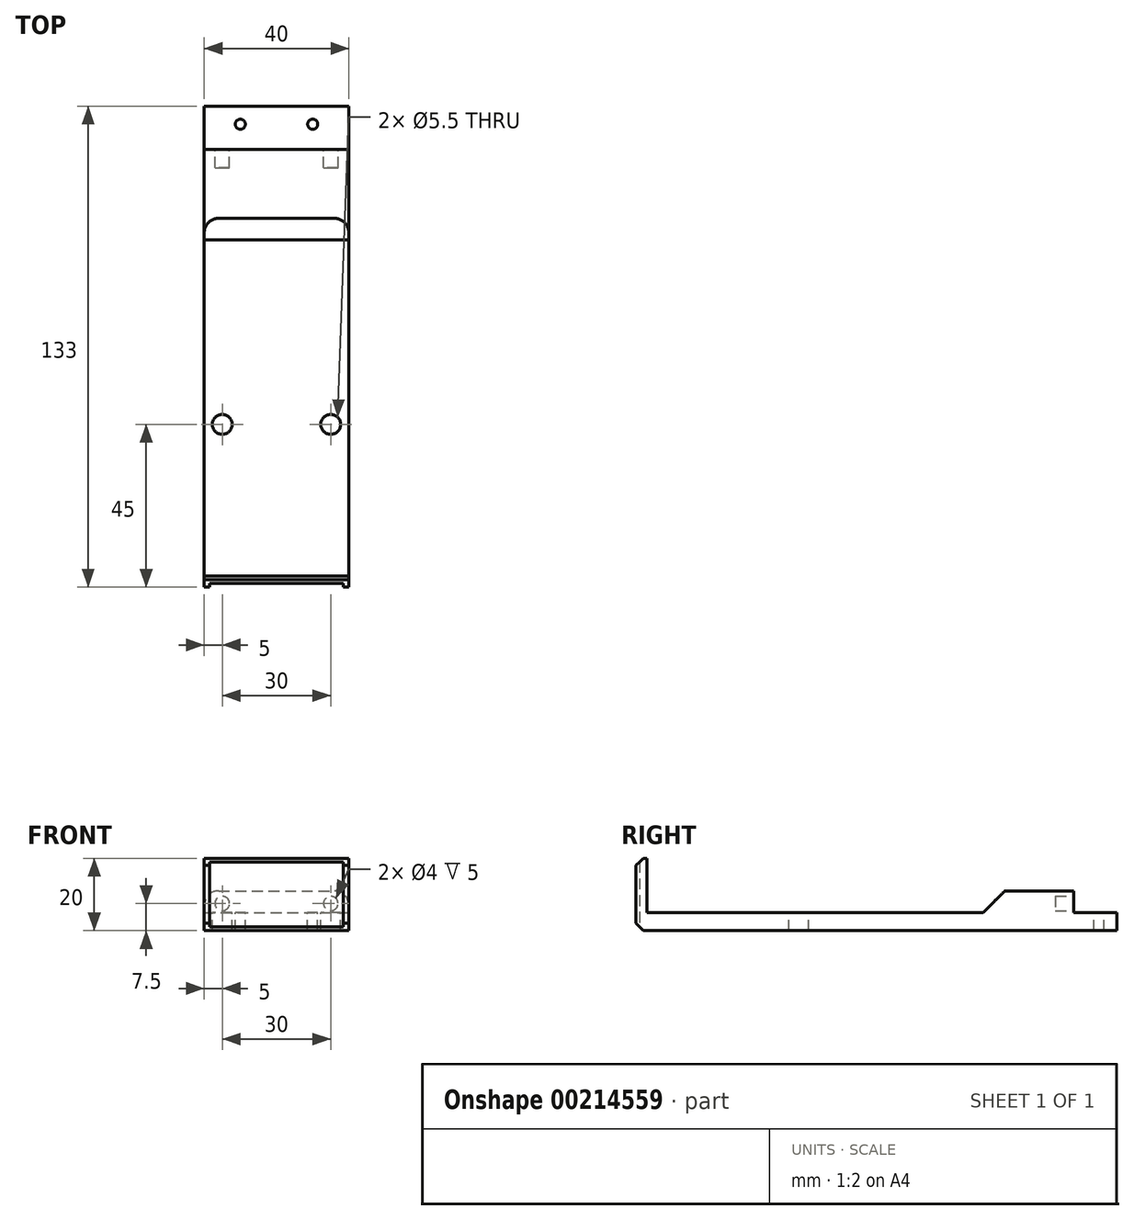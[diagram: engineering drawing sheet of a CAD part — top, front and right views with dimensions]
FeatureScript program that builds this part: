
annotation { "Feature Type Name" : "Feature", "Feature Type Description" : "" }
export const myFeature = defineFeature(function(context is Context, id is Id, definition is map)
    precondition{}
    {
        {
            var Q0;
            Q0=qCreatedBy(makeId("Top.planeOp"),FACE);
            var sketch = newSketch(context, id + "F0", { "sketchPlane" : qUnion([Q0])});
            skLineSegment(sketch, "E0.bottom", {"start": v(-20, 66) * mm, "end": v(20, 66) * mm});
            skLineSegment(sketch, "E0.top", {"start": v(-20, -66) * mm, "end": v(20, -66) * mm});
            skLineSegment(sketch, "E0.left", {"start": v(-20, 66) * mm, "end": v(-20, -66) * mm});
            skLineSegment(sketch, "E0.right", {"start": v(20, 66) * mm, "end": v(20, -66) * mm});
            skSolve(sketch);
        }
        {
            var Q0;
            Q0=makeQuery(id+"F0.imprint","IMPRINT",FACE,{"disambiguationData":[TD([[makeQuery(id+"F0.imprint","IMPRINT",EDGE,{"derivedFrom":sQuery(id+"F0.wireOp",EDGE,"E0.bottom")}),-1.0]])]});
            extrude(context, id + "F1", {"entities" : qUnion([Q0]), "depth" : 5 * mm});
        }
        {
            var Q0;
            Q0=makeQuery(id+"F1.opExtrude","CAP_FACE",FACE,{"disambiguationData":[OSD([sQuery(id+"F0.wireOp",EDGE,"E0.bottom"),sQuery(id+"F0.wireOp",EDGE,"E0.top"),sQuery(id+"F0.wireOp",EDGE,"E0.left"),sQuery(id+"F0.wireOp",EDGE,"E0.right")])],"isStart":false});
            var sketch = newSketch(context, id + "F2", { "sketchPlane" : qUnion([Q0])});
            skLineSegment(sketch, "E1.bottom", {"start": v(-20, -66) * mm, "end": v(20, -66) * mm});
            skLineSegment(sketch, "E1.top", {"start": v(-20, -64) * mm, "end": v(20, -64) * mm});
            skLineSegment(sketch, "E1.left", {"start": v(-20, -66) * mm, "end": v(-20, -64) * mm});
            skLineSegment(sketch, "E1.right", {"start": v(20, -66) * mm, "end": v(20, -64) * mm});
            skPoint(sketch, "E2", {"position": v(-15, -22) * mm});
            skPoint(sketch, "E3", {"position": v(15, -22) * mm});
            skSolve(sketch);
        }
        {
            var Q0;
            Q0=makeQuery(id+"F2.imprint","IMPRINT",FACE,{"disambiguationData":[TD([[makeQuery(id+"F2.imprint","IMPRINT",EDGE,{"derivedFrom":sQuery(id+"F2.wireOp",EDGE,"E1.bottom")}),1.0]])]});
            extrude(context, id + "F3", {"entities" : qUnion([Q0]), "operationType" : NewBodyOperationType.ADD, "depth" : 15 * mm});
        }
        {
            var Q0;
            Q0=sQuery(id+"F2.wireOp",VERTEX,"E2");
            var Q1;
            Q1=sQuery(id+"F2.wireOp",VERTEX,"E3");
            var Q2;
            Q2=makeQuery(id+"F1.opExtrude","SWEPT_BODY",BODY,{"disambiguationData":[OSD([sQuery(id+"F0.wireOp",EDGE,"E0.bottom"),sQuery(id+"F0.wireOp",EDGE,"E0.top"),sQuery(id+"F0.wireOp",EDGE,"E0.left"),sQuery(id+"F0.wireOp",EDGE,"E0.right")])]});
            hole(context, id + "F4", {"style" : HoleStyle.SIMPLE, "endStyle" : HoleEndStyle.BLIND, "holeDiameter" : 5.5 * mm, "holeDepth" : 8 * mm, "locations" : qUnion([Q0, Q1]), "scope" : qUnion([Q2])});
        }
        {
            var Q0;
            Q0=makeQuery(id+"F3.opExtrude","CAP_EDGE",EDGE,{"disambiguationData":[OSD([sQuery(id+"F2.wireOp",EDGE,"E1.bottom")])],"isStart":false});
            var Q1;
            Q1=makeQuery(id+"F4.hole-1.boolean.opBoolean","INTERSECT",EDGE,{"derivedFrom":[makeQuery(id+"F1.opExtrude","CAP_FACE",FACE,{"disambiguationData":[OSD([sQuery(id+"F0.wireOp",EDGE,"E0.bottom"),sQuery(id+"F0.wireOp",EDGE,"E0.top"),sQuery(id+"F0.wireOp",EDGE,"E0.left"),sQuery(id+"F0.wireOp",EDGE,"E0.right")])],"isStart":true}),makeQuery(id+"F4.hole-1.opRevolve","SWEPT_FACE",FACE,{"disambiguationData":[OSD([sQuery(id+"F4.hole-1.sketch.wireOp",EDGE,"core_line_2")])]})]});
            var Q2;
            Q2=makeQuery(id+"F4.hole-0.boolean.opBoolean","INTERSECT",EDGE,{"derivedFrom":[makeQuery(id+"F1.opExtrude","CAP_FACE",FACE,{"disambiguationData":[OSD([sQuery(id+"F0.wireOp",EDGE,"E0.bottom"),sQuery(id+"F0.wireOp",EDGE,"E0.top"),sQuery(id+"F0.wireOp",EDGE,"E0.left"),sQuery(id+"F0.wireOp",EDGE,"E0.right")])],"isStart":true}),makeQuery(id+"F4.hole-0.opRevolve","SWEPT_FACE",FACE,{"disambiguationData":[OSD([sQuery(id+"F4.hole-0.sketch.wireOp",EDGE,"core_line_2")])]})]});
            var Q3;
            Q3=makeQuery(id+"F1.opExtrude","CAP_EDGE",EDGE,{"disambiguationData":[OSD([sQuery(id+"F0.wireOp",EDGE,"E0.top")])],"isStart":true});
            chamfer(context, id + "F5", {"entities" : qUnion([Q0, Q1, Q2, Q3]), "width" : 1 * mm, "tangentPropagation" : true});
        }
        {
            var Q0;
            {var subQ0=sQuery(id+"F2.wireOp",EDGE,"E1.top");Q0=makeQuery(id+"F2.imprint","IMPRINT",FACE,{"disambiguationData":[TD([[makeQuery(id+"F2.imprint","IMPRINT",EDGE,{"derivedFrom":subQ0}),1.0]])]});}
            var sketch = newSketch(context, id + "F6", { "sketchPlane" : qUnion([Q0])});
            skLineSegment(sketch, "E4.bottom", {"start": v(-20, 54) * mm, "end": v(20, 54) * mm});
            skLineSegment(sketch, "E4.top", {"start": v(-20, 29) * mm, "end": v(20, 29) * mm});
            skLineSegment(sketch, "E4.left", {"start": v(-20, 54) * mm, "end": v(-20, 29) * mm});
            skLineSegment(sketch, "E4.right", {"start": v(20, 54) * mm, "end": v(20, 29) * mm});
            skPoint(sketch, "E5", {"position": v(-10, 61) * mm});
            skPoint(sketch, "E6", {"position": v(10, 61) * mm});
            skSolve(sketch);
        }
        {
            var Q0;
            Q0=makeQuery(id+"F6.imprint","IMPRINT",FACE,{"disambiguationData":[TD([[makeQuery(id+"F6.imprint","IMPRINT",EDGE,{"derivedFrom":sQuery(id+"F6.wireOp",EDGE,"E4.bottom")}),-1.0]])]});
            extrude(context, id + "F7", {"entities" : qUnion([Q0]), "operationType" : NewBodyOperationType.ADD, "depth" : 6 * mm});
        }
        {
            var Q0;
            Q0=makeQuery(id+"F7.opExtrude","SWEPT_FACE",FACE,{"disambiguationData":[OSD([sQuery(id+"F6.wireOp",EDGE,"E4.bottom")])]});
            var sketch = newSketch(context, id + "F8", { "sketchPlane" : qUnion([Q0])});
            skCircle(sketch, "E7", {"center": v(-15, 7.5) * mm, "radius": 2 * mm});
            skCircle(sketch, "E8", {"center": v(15, 7.5) * mm, "radius": 2 * mm});
            skSolve(sketch);
        }
        {
            var Q0;
            Q0=makeQuery(id+"F8.imprint","IMPRINT",FACE,{"disambiguationData":[TD([[makeQuery(id+"F8.imprint","IMPRINT",EDGE,{"derivedFrom":sQuery(id+"F8.wireOp",EDGE,"E7")}),1.0]])]});
            var Q1;
            Q1=makeQuery(id+"F8.imprint","IMPRINT",FACE,{"disambiguationData":[TD([[makeQuery(id+"F8.imprint","IMPRINT",EDGE,{"derivedFrom":sQuery(id+"F8.wireOp",EDGE,"E8")}),1.0]])]});
            extrude(context, id + "F9", {"entities" : qUnion([Q0, Q1]), "operationType" : NewBodyOperationType.REMOVE, "oppositeDirection" : true, "depth" : 5 * mm});
        }
        {
            var Q0;
            Q0=makeQuery(id+"F7.opExtrude","CAP_EDGE",EDGE,{"disambiguationData":[OSD([sQuery(id+"F6.wireOp",EDGE,"E4.top")])],"isStart":false});
            chamfer(context, id + "F10", {"entities" : qUnion([Q0]), "width" : 6 * mm, "tangentPropagation" : true});
        }
        {
            var Q0;
            Q0=makeQuery(id+"F7.opExtrude","CAP_EDGE",EDGE,{"disambiguationData":[OSD([sQuery(id+"F6.wireOp",EDGE,"E4.left")])],"isStart":false});
            var Q1;
            Q1=makeQuery(id+"F7.opExtrude","CAP_EDGE",EDGE,{"disambiguationData":[OSD([sQuery(id+"F6.wireOp",EDGE,"E4.right")])],"isStart":false});
            fillet(context, id + "F11", {"entities" : qUnion([Q0, Q1]), "radius" : 4 * mm, "tangentPropagation" : true, "allowEdgeOverflow" : false});
        }
        {
            var Q0;
            Q0=sQuery(id+"F6.wireOp",VERTEX,"E6");
            var Q1;
            Q1=sQuery(id+"F6.wireOp",VERTEX,"E5");
            var Q2;
            Q2=makeQuery(id+"F1.opExtrude","SWEPT_BODY",BODY,{"disambiguationData":[OSD([sQuery(id+"F0.wireOp",EDGE,"E0.bottom"),sQuery(id+"F0.wireOp",EDGE,"E0.top"),sQuery(id+"F0.wireOp",EDGE,"E0.left"),sQuery(id+"F0.wireOp",EDGE,"E0.right")])]});
            hole(context, id + "F12", {"style" : HoleStyle.SIMPLE, "endStyle" : HoleEndStyle.BLIND, "holeDiameter" : 2.8 * mm, "holeDepth" : 8 * mm, "locations" : qUnion([Q0, Q1]), "scope" : qUnion([Q2])});
        }
        {
            var Q0;
            Q0=makeQuery(id+"F3.boolean.opBoolean","MERGE",FACE,{"derivedFrom":[makeQuery(id+"F1.opExtrude","SWEPT_FACE",FACE,{"disambiguationData":[OSD([sQuery(id+"F0.wireOp",EDGE,"E0.top")])]}),makeQuery(id+"F3.opExtrude","SWEPT_FACE",FACE,{"disambiguationData":[OSD([sQuery(id+"F2.wireOp",EDGE,"E1.bottom")])]})]});
            var sketch = newSketch(context, id + "F13", { "sketchPlane" : qUnion([Q0])});
            skLineSegment(sketch, "E9.bottom", {"start": v(-20, 19) * mm, "end": v(-18.5, 19) * mm});
            skLineSegment(sketch, "E9.top", {"start": v(-20, 1) * mm, "end": v(-18.5, 1) * mm});
            skLineSegment(sketch, "E9.left", {"start": v(-20, 19) * mm, "end": v(-20, 1) * mm});
            skLineSegment(sketch, "E9.right", {"start": v(-18.5, 19) * mm, "end": v(-18.5, 1) * mm});
            skLineSegment(sketch, "E10.bottom", {"start": v(20, 19) * mm, "end": v(18.5, 19) * mm});
            skLineSegment(sketch, "E10.top", {"start": v(20, 1) * mm, "end": v(18.5, 1) * mm});
            skLineSegment(sketch, "E10.left", {"start": v(20, 19) * mm, "end": v(20, 1) * mm});
            skLineSegment(sketch, "E10.right", {"start": v(18.5, 19) * mm, "end": v(18.5, 1) * mm});
            skSolve(sketch);
        }
        {
            var Q0;
            Q0=makeQuery(id+"F13.imprint","IMPRINT",FACE,{"disambiguationData":[TD([[makeQuery(id+"F13.imprint","IMPRINT",EDGE,{"derivedFrom":sQuery(id+"F13.wireOp",EDGE,"E9.bottom")}),1.0]])]});
            var Q1;
            Q1=makeQuery(id+"F13.imprint","IMPRINT",FACE,{"disambiguationData":[TD([[makeQuery(id+"F13.imprint","IMPRINT",EDGE,{"derivedFrom":sQuery(id+"F13.wireOp",EDGE,"E10.bottom")}),1.0]])]});
            extrude(context, id + "F14", {"entities" : qUnion([Q0, Q1]), "operationType" : NewBodyOperationType.ADD, "depth" : 1 * mm});
        }
        {
            var Q0;
            Q0=makeQuery(id+"F14.opExtrude","CAP_EDGE",EDGE,{"disambiguationData":[OSD([sQuery(id+"F13.wireOp",EDGE,"E9.bottom")])],"isStart":false});
            var Q1;
            Q1=makeQuery(id+"F14.opExtrude","CAP_EDGE",EDGE,{"disambiguationData":[OSD([sQuery(id+"F13.wireOp",EDGE,"E9.top")])],"isStart":false});
            var Q2;
            Q2=makeQuery(id+"F14.opExtrude","CAP_EDGE",EDGE,{"disambiguationData":[OSD([sQuery(id+"F13.wireOp",EDGE,"E10.bottom")])],"isStart":false});
            var Q3;
            Q3=makeQuery(id+"F14.opExtrude","CAP_EDGE",EDGE,{"disambiguationData":[OSD([sQuery(id+"F13.wireOp",EDGE,"E10.top")])],"isStart":false});
            chamfer(context, id + "F15", {"entities" : qUnion([Q0, Q1, Q2, Q3]), "width" : 1 * mm, "tangentPropagation" : true});
        }
    });
